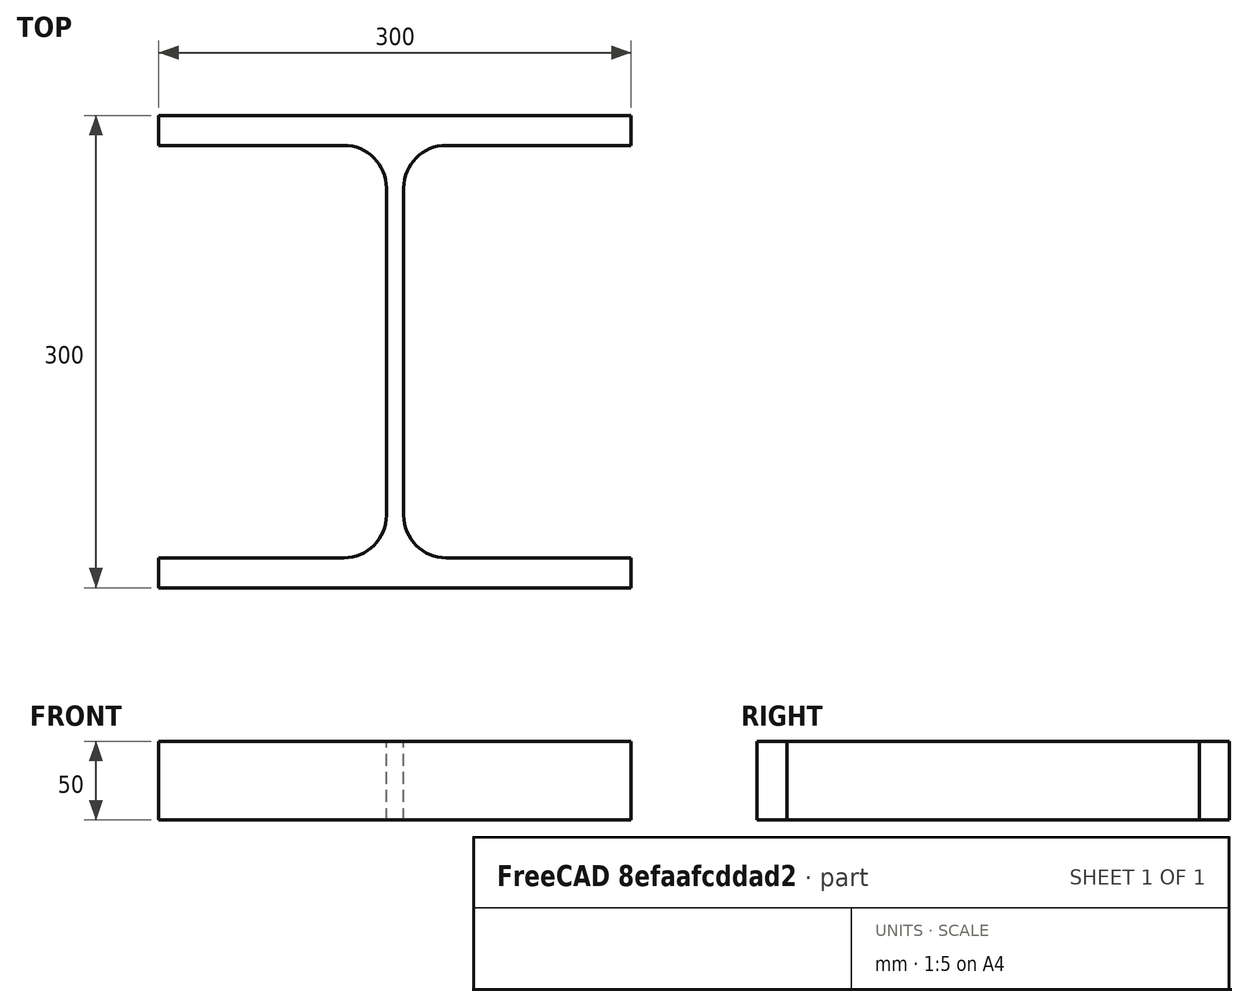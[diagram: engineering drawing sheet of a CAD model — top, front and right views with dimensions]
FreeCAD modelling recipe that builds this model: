
FCSTD DOCUMENT  (FreeCAD 0.15R4671 (Git))
Label: HE-B-Profile 300 DIN1025-2 S235JR
License: All rights reserved
LicenseURL: http://en.wikipedia.org/wiki/All_rights_reserved
objects: Sketcher::SketchObject×1, Part::Extrusion×1
note: 2 computed .brp shape members not serialized (recipe doc carries the construction recipe); baked Part::Feature solids carry a one-line shape summary decoded from their .brp

FEATURE [Sketcher::SketchObject] Sketch
  sketch-geometry (16):
    g0: LineSegment StartX=5.5 StartY=-104 StartZ=0 EndX=5.5 EndY=104 EndZ=0
    g1: LineSegment StartX=32.5 StartY=131 StartZ=0 EndX=150 EndY=131 EndZ=0
    g2: LineSegment StartX=150 StartY=131 StartZ=0 EndX=150 EndY=150 EndZ=0
    g3: LineSegment StartX=150 StartY=150 StartZ=0 EndX=-150 EndY=150 EndZ=0
    g4: LineSegment StartX=-150 StartY=150 StartZ=0 EndX=-150 EndY=131 EndZ=0
    g5: LineSegment StartX=-150 StartY=131 StartZ=0 EndX=-32.5 EndY=131 EndZ=0
    g6: LineSegment StartX=-5.5 StartY=104 StartZ=0 EndX=-5.5 EndY=-104 EndZ=0
    g7: LineSegment StartX=-32.5 StartY=-131 StartZ=0 EndX=-150 EndY=-131 EndZ=0
    g8: LineSegment StartX=-150 StartY=-131 StartZ=0 EndX=-150 EndY=-150 EndZ=0
    g9: LineSegment StartX=-150 StartY=-150 StartZ=0 EndX=150 EndY=-150 EndZ=0
    g10: LineSegment StartX=150 StartY=-150 StartZ=0 EndX=150 EndY=-131 EndZ=0
    g11: LineSegment StartX=150 StartY=-131 StartZ=0 EndX=32.5 EndY=-131 EndZ=0
    g12: ArcOfCircle CenterX=32.5 CenterY=104 CenterZ=0 NormalX=0 NormalY=0 NormalZ=1 Radius=27 StartAngle=1.5708 EndAngle=3.14159
    g13: ArcOfCircle CenterX=32.5 CenterY=-104 CenterZ=0 NormalX=0 NormalY=0 NormalZ=1 Radius=27 StartAngle=3.14159 EndAngle=4.71239
    g14: ArcOfCircle CenterX=-32.5 CenterY=104 CenterZ=0 NormalX=0 NormalY=0 NormalZ=1 Radius=27 StartAngle=0 EndAngle=1.5708
    g15: ArcOfCircle CenterX=-32.5 CenterY=-104 CenterZ=0 NormalX=0 NormalY=0 NormalZ=1 Radius=27 StartAngle=4.71239 EndAngle=6.28319
  constraints (42):
    c: Vertical(g0)
    c: Coincident(g2,g1)
    c: Vertical(g2)
    c: Coincident(g3,g2)
    c: Coincident(g4,g3)
    c: Vertical(g4)
    c: Coincident(g5,g4)
    c: Horizontal(g5)
    c: Vertical(g6)
    c: Horizontal(g7)
    c: Coincident(g8,g7)
    c: Vertical(g8)
    c: Coincident(g9,g8)
    c: Horizontal(g9)
    c: Coincident(g10,g9)
    c: Vertical(g10)
    c: Coincident(g11,g10)
    c: Horizontal(g11)
    c: Tangent(g1,g12) = 1.5708
    c: Tangent(g0,g12) = 1.5708
    c: Tangent(g0,g13) = 1.5708
    c: Tangent(g11,g13) = 1.5708
    c: Tangent(g5,g14) = 1.5708
    c: Tangent(g6,g14) = 1.5708
    c: Tangent(g6,g15) = 1.5708
    c: Tangent(g7,g15) = 1.5708
    c: Equal(g3,g9)
    c: Equal(g2,g4)
    c: Equal(g4,g8)
    c: Equal(g8,g10)
    c: Equal(g12,g14)
    c: Equal(g14,g15)
    c: Equal(g15,g13)
    c: Symmetric(g2,g3,g-2)
    c: Symmetric(g9,g8,g-2)
    c: Symmetric(g0,g6,g-2)
    c: Symmetric(g2,g9,g-1)
    c: DistanceY(g2,g9) = -300
    c: DistanceX(g3) = -300
    c: DistanceX(g0,g6) = -11
    c: DistanceY(g2) = 19
    c: Radius(g12) = 27
FEATURE [Part::Extrusion] Extrude  label="HE-B-Profile 300 DIN1025-2 S235JR"
  Base = -> Sketch
  Dir = (0,0,50)
  Solid = true
